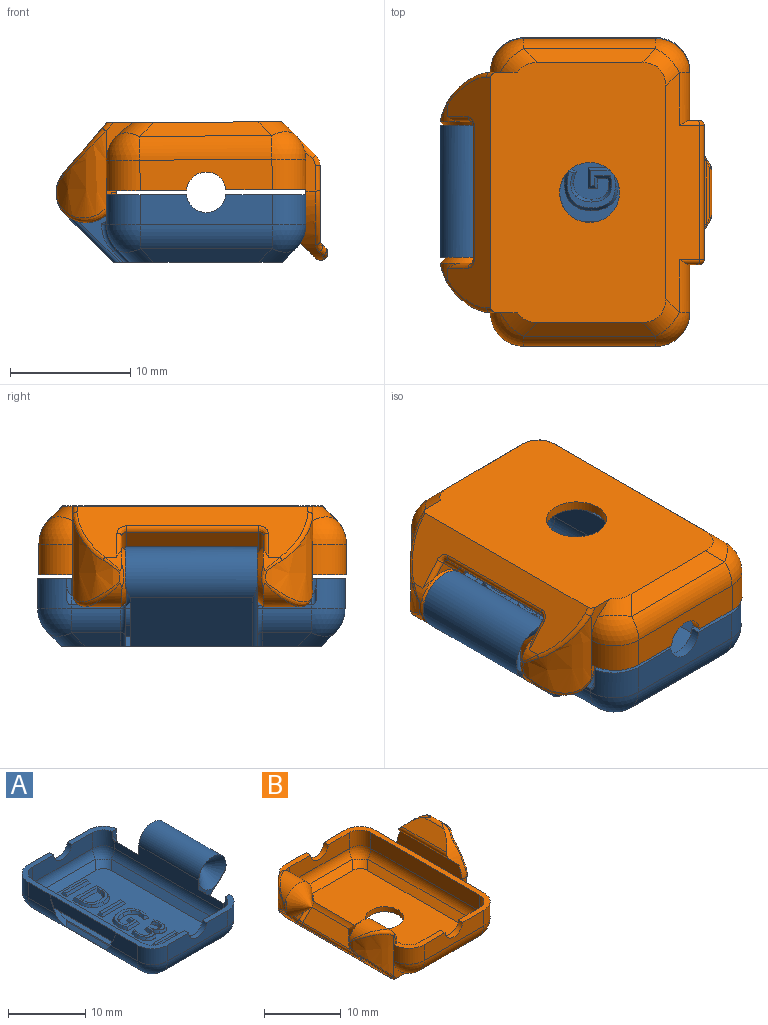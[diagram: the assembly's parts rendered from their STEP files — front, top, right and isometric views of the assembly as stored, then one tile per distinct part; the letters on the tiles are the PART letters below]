
ASSEMBLY  parts=2 mates=1
PART A: 172 faces, bbox 21.2x25.8x8.8 mm
  f0: plane 21.17x12.17mm, normal (0,0,1), area 198.2mm2, adj f18,f19,f20,f21,f22,f23,f24,f25
  f1: cylinder r=2mm len=20mm, axis (0,1,0), area 20.4mm2, adj f4,f21,f36,f38,f69,f71,f72
  f2: cylinder r=2.8mm len=20mm, axis (0,1,0), area 28.1mm2, adj f3,f28,f42,f44,f48,f71,f72,f74
  f3: plane 5.02x2.6mm, normal (-1,0,0), area 11mm2, adj f2,f5,f47,f71
  f4: plane 20x2.52mm, normal (1,0,0), area 50.3mm2, adj f1,f5,f53,f54,f70,f71,f72
  f5: plane 25.6x6.66mm, normal (0,0,1), area 27mm2, adj f3,f4,f46,f47,f48,f49,f50,f51
  f6: plane 4.1x1.15mm, normal (0.71,0,-0.71), area 5.7mm2, adj f10,f17,f30,f167
  f7: plane 4.1x1.15mm, normal (0.71,0,-0.71), area 5.7mm2, adj f11,f17,f32,f162
  f8: plane 4.1x0.32mm, normal (1,0,0), area 1.3mm2, adj f10,f12,f63,f165
  f9: plane 4.1x0.32mm, normal (1,0,0), area 1.3mm2, adj f11,f13,f61,f164
  f10: cylinder r=2.8mm len=4.1mm, axis (0,-1,0), area 9mm2, adj f6,f8,f43,f166
  f11: cylinder r=2.8mm len=4.1mm, axis (0,-1,0), area 9mm2, adj f7,f9,f45,f163
  f12: cylinder r=2.8mm len=2.8mm, axis (0,0,1), area 10.3mm2, adj f8,f43,f49,f58,f64,f171
  f13: cylinder r=2.8mm len=2.8mm, axis (0,0,-1), area 10.3mm2, adj f9,f16,f45,f50,f60,f170
  f14: cylinder r=2mm len=2.52mm, axis (0,0,1), area 7.5mm2, adj f37,f55,f56,f58,f171
  f15: cylinder r=2mm len=2.52mm, axis (0,0,-1), area 7.5mm2, adj f16,f39,f56,f57,f170
  f16: plane 6.63x2.4mm, normal (0,0,1), area 5.8mm2, adj f13,f15,f50,f51,f57,f60,f170
  f17: plane 21.83x14.24mm, normal (0,0,-1), area 286.8mm2, adj f6,f7,f26,f27,f28,f29,f30,f31
  f18: plane 11x0.91mm, normal (0,-0.71,0.71), area 13mm2, adj f0,f24,f25,f33
  f19: plane 20x0.91mm, normal (-0.71,0,0.71), area 24.7mm2, adj f0,f23,f25,f34
  f20: plane 11x0.91mm, normal (0,0.71,0.71), area 13mm2, adj f0,f22,f23,f35
  f21: plane 20x0.91mm, normal (0.71,0,0.71), area 24.7mm2, adj f0,f1,f22,f24
  f22: cylinder r=2mm len=2.33mm, axis (0.58,0.58,-0.58), area 2.8mm2, adj f0,f20,f21,f36
  f23: cylinder r=2mm len=2.33mm, axis (0.58,-0.58,0.58), area 2.8mm2, adj f0,f19,f20,f37
  f24: cylinder r=2mm len=2.33mm, axis (0.58,-0.58,-0.58), area 2.8mm2, adj f0,f18,f21,f38
  f25: cylinder r=2mm len=2.33mm, axis (0.58,0.58,0.58), area 2.8mm2, adj f0,f18,f19,f39
  f26: plane 11x1.15mm, normal (0,0.71,-0.71), area 16mm2, adj f17,f31,f32,f40
  f27: plane 11x1.15mm, normal (0,-0.71,-0.71), area 16mm2, adj f17,f29,f30,f41
  f28: plane 20x1.15mm, normal (-0.71,0,-0.71), area 30.6mm2, adj f2,f17,f29,f31
  f29: cylinder r=2.8mm len=3.13mm, axis (0.58,0.58,-0.58), area 4.8mm2, adj f17,f27,f28,f42
  f30: cylinder r=2.8mm len=3.13mm, axis (0.58,-0.58,0.58), area 4.8mm2, adj f6,f17,f27,f43
  f31: cylinder r=2.8mm len=3.13mm, axis (0.58,-0.58,-0.58), area 4.8mm2, adj f17,f26,f28,f44
  f32: cylinder r=2.8mm len=3.13mm, axis (0.58,0.58,0.58), area 4.8mm2, adj f7,f17,f26,f45
  f33: cylinder r=2mm len=11mm, axis (1,0,0), area 17.3mm2, adj f18,f38,f39,f57
  f34: cylinder r=2mm len=20mm, axis (0,-1,0), area 31.4mm2, adj f19,f37,f39,f56
  f35: cylinder r=2mm len=11mm, axis (-1,0,0), area 17.3mm2, adj f20,f36,f37,f55
  f36: sphere r=2mm, area 4.9mm2, adj f1,f22,f35,f53
  f37: sphere r=2mm, area 4.9mm2, adj f14,f23,f34,f35
  f38: sphere r=2mm, area 4.9mm2, adj f1,f24,f33,f54
  f39: sphere r=2mm, area 4.9mm2, adj f15,f25,f33,f34
  f40: cylinder r=2.8mm len=11mm, axis (1,0,0), area 24.2mm2, adj f26,f44,f45,f50
  f41: cylinder r=2.8mm len=11mm, axis (-1,0,0), area 24.2mm2, adj f27,f42,f43,f49
  f42: sphere r=2.8mm, area 9.7mm2, adj f2,f29,f41,f46
  f43: sphere r=2.8mm, area 9.7mm2, adj f10,f12,f30,f41
  f44: sphere r=2.8mm, area 9.7mm2, adj f2,f31,f40,f47
  f45: sphere r=2.8mm, area 9.7mm2, adj f11,f13,f32,f40
  f46: cylinder r=2.8mm len=2.8mm, axis (0,0,-1), area 11.1mm2, adj f5,f42,f48,f49
  f47: cylinder r=2.8mm len=2.8mm, axis (0,0,1), area 11.1mm2, adj f3,f5,f44,f50
  f48: plane 5.02x2.6mm, normal (-1,0,0), area 11mm2, adj f2,f5,f46,f72
  f49: plane 11x2.52mm, normal (0,-1,0), area 24mm2, adj f5,f12,f41,f46,f52,f58
  f50: plane 11x2.52mm, normal (0,1,0), area 24mm2, adj f5,f13,f16,f40,f47,f51
  f51: cylinder r=1.65mm len=3.29mm, axis (0,1,0), area 3.9mm2, adj f5,f16,f50,f57
  f52: cylinder r=1.65mm len=3.29mm, axis (0,1,0), area 3.9mm2, adj f5,f49,f55,f58
  f53: cylinder r=2mm len=2.52mm, axis (0,0,-1), area 7.9mm2, adj f4,f5,f36,f55
  f54: cylinder r=2mm len=2.52mm, axis (0,0,1), area 7.9mm2, adj f4,f5,f38,f57
  f55: plane 11x2.52mm, normal (0,1,0), area 24mm2, adj f5,f14,f35,f52,f53,f58
  f56: plane 20x2.67mm, normal (-1,0,0), area 40.2mm2, adj f14,f15,f34,f59,f61,f62,f63,f67
  f57: plane 11x2.52mm, normal (0,-1,0), area 24mm2, adj f5,f15,f16,f33,f51,f54
  f58: plane 6.63x2.4mm, normal (0,0,1), area 5.8mm2, adj f12,f14,f49,f52,f55,f64,f171
  f59: plane 5.8x3.63mm, normal (0,1,0), area 3.2mm2, adj f17,f56,f61,f65,f162,f163,f164,f169
  f60: plane 1.66x0.77mm, normal (0,-1,0), area 0.8mm2, adj f13,f16,f170
  f61: cylinder r=2.9mm len=4.5mm, axis (0,1,0), area 5.4mm2, adj f9,f56,f59,f164,f170
  f62: plane 5.8x3.63mm, normal (0,-1,0), area 3.2mm2, adj f17,f56,f63,f66,f165,f166,f167,f168
  f63: cylinder r=2.9mm len=4.5mm, axis (0,1,0), area 5.4mm2, adj f8,f56,f62,f165,f171
  f64: plane 1.66x0.77mm, normal (0,1,0), area 0.8mm2, adj f12,f58,f171
  f65: cone r=2.5mm half-angle=45deg, axis (0,1,0), area 27.5mm2, adj f59,f67,f169
  f66: cone r=2.5mm half-angle=45deg, axis (0,-1,0), area 27.5mm2, adj f62,f67,f168
  f67: cylinder r=2.5mm len=11mm, axis (0,1,0), area 107.4mm2, adj f56,f65,f66,f68,f168,f169
  f68: plane 10.2x4.03mm, normal (0.71,0,-0.71), area 58.2mm2, adj f17,f67,f168,f169
  f69: cylinder r=0.7mm len=8.33mm, axis (0,1,0), area 1.2mm2, adj f1,f71,f72,f74
  f70: plane 10.87x0.71mm, normal (-0.71,0,-0.71), area 10.4mm2, adj f4,f71,f72,f73
  f71: extruded ~4.23x2.39mm, area 2.1mm2, adj f1,f2,f3,f4,f5,f69,f70,f73
  f72: extruded ~4.23x2.39mm, area 2.1mm2, adj f1,f2,f4,f5,f48,f69,f70,f73
  f73: plane 11.99x1.81mm, normal (-1,0,0), area 20.9mm2, adj f5,f70,f71,f72
  f74: plane 8.15x0.49mm, normal (-0.71,0,0.71), area 5.2mm2, adj f2,f69,f71,f72
  f75: plane 4.35x0.4mm, normal (0,0.87,0.5), area 1.9mm2, adj f0,f76,f78,f79
  f76: plane 0.92x0.4mm, normal (-0.87,0,0.5), area 0.3mm2, adj f0,f75,f77,f79
  f77: plane 4.35x0.4mm, normal (0,-0.87,0.5), area 1.9mm2, adj f0,f76,f78,f79
  f78: plane 0.92x0.4mm, normal (0.87,0,0.5), area 0.3mm2, adj f0,f75,f77,f79
  f79: plane 3.89x0.46mm, normal (0,0,1), area 1.8mm2, adj f75,f76,f77,f78
  f80: bspline ~1.68x1.52mm, area 1.1mm2, adj f81,f91,f92,f93
  f81: bspline ~1.71x1.61mm, area 1.1mm2, adj f80,f82,f92,f93
  f82: plane 0.63x0.4mm, normal (0.87,0,0.5), area 0.2mm2, adj f81,f83,f92,f93
  f83: plane 3.3x0.4mm, normal (0,-0.87,0.5), area 1.4mm2, adj f82,f91,f92,f93
  f84: bspline ~1.65x0.8mm, area 0.8mm2, adj f0,f85,f90,f92
  f85: bspline ~1.57x0.78mm, area 0.8mm2, adj f0,f84,f86,f92
  f86: bspline ~1.66x0.76mm, area 0.8mm2, adj f0,f85,f87,f92
  f87: plane 1.37x0.4mm, normal (0.87,0,0.5), area 0.6mm2, adj f0,f86,f88,f92
  f88: plane 4.35x0.4mm, normal (0,0.87,0.5), area 1.9mm2, adj f0,f87,f89,f92
  f89: plane 1.23x0.4mm, normal (-0.87,0,0.5), area 0.5mm2, adj f0,f88,f90,f92
  f90: bspline ~1.77x0.77mm, area 0.8mm2, adj f0,f84,f89,f92
  f91: plane 0.72x0.4mm, normal (-0.87,0,0.5), area 0.3mm2, adj f80,f83,f92,f93
  f92: plane 4.09x3.34mm, normal (0,0,1), area 4.5mm2, adj f80,f81,f82,f83,f84,f85,f86,f87
  f93: plane 3.02x1.91mm, normal (0,0,1), area 4.3mm2, adj f80,f81,f82,f83,f91
  f94: plane 4.35x0.4mm, normal (0,0.87,0.5), area 1.9mm2, adj f0,f95,f97,f98
  f95: plane 0.92x0.4mm, normal (-0.87,0,0.5), area 0.3mm2, adj f0,f94,f96,f98
  f96: plane 4.35x0.4mm, normal (0,-0.87,0.5), area 1.9mm2, adj f0,f95,f97,f98
  f97: plane 0.92x0.4mm, normal (0.87,0,0.5), area 0.3mm2, adj f0,f94,f96,f98
  f98: plane 3.89x0.46mm, normal (0,0,1), area 1.8mm2, adj f94,f95,f96,f97
  f99: plane 1.73x0.4mm, normal (0.87,0,0.5), area 0.7mm2, adj f0,f100,f117,f118
  f100: plane 0.77x0.4mm, normal (0,0.87,0.5), area 0.2mm2, adj f0,f99,f101,f118
  f101: plane 1.06x0.4mm, normal (-0.87,0,0.5), area 0.4mm2, adj f0,f100,f102,f118
  f102: plane 1.34x0.41mm, normal (0,0.87,0.5), area 0.5mm2, adj f0,f101,f103,f118
  f103: bspline ~0.83x0.48mm, area 0.3mm2, adj f0,f102,f104,f118
  f104: bspline ~1.06x0.65mm, area 0.5mm2, adj f0,f103,f105,f118
  f105: bspline ~1.25x0.57mm, area 0.6mm2, adj f0,f104,f106,f118
  f106: bspline ~1.27x0.64mm, area 0.6mm2, adj f0,f105,f107,f118
  f107: bspline ~1.16x0.68mm, area 0.5mm2, adj f0,f106,f108,f118
  f108: bspline ~1.12x0.52mm, area 0.5mm2, adj f0,f107,f109,f118
  f109: plane 0.92x0.61mm, normal (-0.33,-0.8,0.5), area 0.3mm2, adj f0,f108,f110,f118
  f110: bspline ~1.29x0.52mm, area 0.6mm2, adj f0,f109,f111,f118
  f111: bspline ~1.67x0.79mm, area 0.8mm2, adj f0,f110,f112,f118
  f112: bspline ~1.64x0.8mm, area 0.8mm2, adj f0,f111,f113,f118
  f113: bspline ~1.66x0.73mm, area 0.8mm2, adj f0,f112,f114,f118
  f114: bspline ~1.5x0.76mm, area 0.7mm2, adj f0,f113,f115,f118
  f115: bspline ~0.76x0.48mm, area 0.3mm2, adj f0,f114,f116,f118
  f116: bspline ~0.83x0.48mm, area 0.4mm2, adj f0,f115,f117,f118
  f117: plane 2.44x0.58mm, normal (0,-0.87,0.5), area 0.9mm2, adj f0,f99,f116,f118
  f118: plane 4.2x3.3mm, normal (0,0,1), area 4.1mm2, adj f99,f100,f101,f102,f103,f104,f105,f106
  f119: plane 2.74x2.47mm, normal (0,0,1), area 1.6mm2, adj f129,f130,f131,f132,f133,f134,f135,f136
  f120: bspline ~0.69x0.48mm, area 0.3mm2, adj f0,f121,f146,f147
  f121: bspline ~0.76x0.55mm, area 0.4mm2, adj f0,f120,f122,f147
  f122: bspline ~1.07x0.5mm, area 0.5mm2, adj f0,f121,f123,f147
  f123: bspline ~1.42x0.65mm, area 0.7mm2, adj f0,f122,f124,f147
  f124: plane 0.82x0.68mm, normal (-0.48,0.72,0.5), area 0.2mm2, adj f0,f123,f125,f147
  f125: bspline ~0.64x0.51mm, area 0.2mm2, adj f0,f124,f126,f147
  f126: bspline ~0.52x0.48mm, area 0.2mm2, adj f0,f125,f127,f147
  f127: bspline ~0.9x0.77mm, area 0.5mm2, adj f0,f126,f128,f147
  f128: bspline ~0.69x0.51mm, area 0.3mm2, adj f0,f127,f129,f147
  f129: bspline ~0.88x0.48mm, area 0.4mm2, adj f0,f119,f128,f130,f145,f146,f147
  f130: plane 0.4x0.34mm, normal (0.87,0,0.5), area 0.1mm2, adj f0,f119,f129,f131
  f131: plane 0.71x0.4mm, normal (0,0.87,0.5), area 0.2mm2, adj f0,f119,f130,f132
  f132: plane 0.4x0.33mm, normal (-0.87,0,0.5), area 0.1mm2, adj f0,f119,f131,f133
  f133: bspline ~0.92x0.48mm, area 0.4mm2, adj f0,f119,f132,f134
  f134: bspline ~0.68x0.53mm, area 0.3mm2, adj f0,f119,f133,f135
  f135: bspline ~0.72x0.49mm, area 0.3mm2, adj f0,f119,f134,f136
  f136: bspline ~0.83x0.48mm, area 0.4mm2, adj f0,f119,f135,f137
  f137: bspline ~0.67x0.48mm, area 0.3mm2, adj f0,f119,f136,f138
  f138: bspline ~0.68x0.48mm, area 0.2mm2, adj f0,f119,f137,f139
  f139: plane 0.97x0.58mm, normal (0,0.87,0.5), area 0.2mm2, adj f0,f119,f138,f140
  f140: bspline ~1.26x0.49mm, area 0.6mm2, adj f0,f119,f139,f141
  f141: bspline ~1.3x0.57mm, area 0.6mm2, adj f0,f119,f140,f142
  f142: bspline ~0.98x0.62mm, area 0.5mm2, adj f0,f119,f141,f143
  f143: bspline ~0.69x0.48mm, area 0.3mm2, adj f0,f119,f142,f144
  f144: bspline ~1.04x0.55mm, area 0.4mm2, adj f0,f119,f143,f145
  f145: plane 0.43x0.43mm, normal (0,-0.87,0.5), area 0.1mm2, adj f0,f119,f129,f144,f146
  f146: bspline ~0.94x0.62mm, area 0.4mm2, adj f0,f120,f129,f145,f147
  f147: plane 2.51x1.87mm, normal (0,0,1), area 1.1mm2, adj f120,f121,f122,f123,f124,f125,f126,f127
  f148: bspline ~1.68x1.52mm, area 1.1mm2, adj f149,f159,f160,f161
  f149: bspline ~1.71x1.61mm, area 1.1mm2, adj f148,f150,f160,f161
  f150: plane 0.63x0.4mm, normal (0.87,0,0.5), area 0.2mm2, adj f149,f151,f160,f161
  f151: plane 3.3x0.4mm, normal (0,-0.87,0.5), area 1.4mm2, adj f150,f159,f160,f161
  f152: bspline ~1.65x0.8mm, area 0.8mm2, adj f0,f153,f158,f160
  f153: bspline ~1.57x0.78mm, area 0.8mm2, adj f0,f152,f154,f160
  f154: bspline ~1.66x0.76mm, area 0.8mm2, adj f0,f153,f155,f160
  f155: plane 1.37x0.4mm, normal (0.87,0,0.5), area 0.6mm2, adj f0,f154,f156,f160
  f156: plane 4.35x0.4mm, normal (0,0.87,0.5), area 1.9mm2, adj f0,f155,f157,f160
  f157: plane 1.23x0.4mm, normal (-0.87,0,0.5), area 0.5mm2, adj f0,f156,f158,f160
  f158: bspline ~1.77x0.77mm, area 0.8mm2, adj f0,f152,f157,f160
  f159: plane 0.72x0.4mm, normal (-0.87,0,0.5), area 0.3mm2, adj f148,f151,f160,f161
  f160: plane 4.09x3.34mm, normal (0,0,1), area 4.5mm2, adj f148,f149,f150,f151,f152,f153,f154,f155
  f161: plane 3.02x1.91mm, normal (0,0,1), area 4.3mm2, adj f148,f149,f150,f151,f159
  f162: cylinder r=0.4mm len=1.43mm, axis (0.71,0,0.71), area 0.9mm2, adj f7,f17,f59,f163
  f163: torus R=3.2mm, axis (0,1,0), area 1.5mm2, adj f11,f59,f162,f164
  f164: cylinder r=0.4mm len=0.4mm, axis (0,0,1), area 0.1mm2, adj f9,f59,f61,f163
  f165: cylinder r=0.4mm len=0.4mm, axis (0,0,1), area 0.1mm2, adj f8,f62,f63,f166
  f166: torus R=3.2mm, axis (0,1,0), area 1.5mm2, adj f10,f62,f165,f167
  f167: cylinder r=0.4mm len=1.43mm, axis (0.71,0,0.71), area 0.9mm2, adj f6,f17,f62,f166
  f168: cylinder r=0.4mm len=5.56mm, axis (-0.71,0,-0.71), area 3.5mm2, adj f17,f62,f66,f67,f68
  f169: cylinder r=0.4mm len=5.56mm, axis (-0.71,0,-0.71), area 3.5mm2, adj f17,f59,f65,f67,f68
  f170: torus R=2.5mm, axis (0,-1,0), area 0.9mm2, adj f13,f15,f16,f60,f61
  f171: torus R=2.5mm, axis (0,-1,0), area 0.9mm2, adj f12,f14,f58,f63,f64
PART B: 122 faces, bbox 24.2x26.7x12.9 mm
  f0: plane 19.29x4.24mm, normal (-0.75,0,-0.66), area 55.2mm2, adj f2,f17,f18,f99,f100,f106,f107,f115
  f1: cylinder r=2.5mm len=4.94mm, axis (0,1,0), area 19.8mm2, adj f5,f24,f102,f103,f104
  f2: cylinder r=2.5mm len=1.86mm, axis (0,1,0), area 1.2mm2, adj f0,f5,f101,f102,f121
  f3: cylinder r=2.5mm len=4.94mm, axis (0,1,0), area 19.8mm2, adj f22,f24,f109,f110,f111
  f4: plane 3.16x2.29mm, normal (0,1,0), area 2mm2, adj f17,f67,f69,f81,f99
  f5: cone r=2.5mm half-angle=45deg, axis (0,1,0), area 27.8mm2, adj f1,f2,f73,f102,f116
  f6: plane 3.16x2.29mm, normal (0,-1,0), area 2mm2, adj f17,f62,f64,f80,f106
  f7: plane 12x2.18mm, normal (-1,0,0), area 25mm2, adj f12,f14,f72,f76,f77,f78
  f8: plane 5.15x0.31mm, normal (0.71,0,-0.71), area 2mm2, adj f9,f88,f92,f93
  f9: cylinder r=0.6mm len=4.18mm, axis (0,1,0), area 5.7mm2, adj f8,f10,f77,f78,f86,f90
  f10: plane 8.62x2.13mm, normal (-0.71,0,0.71), area 15.8mm2, adj f9,f11,f77,f78
  f11: cylinder r=0.6mm len=9.6mm, axis (0,1,0), area 8.4mm2, adj f10,f12,f77,f78
  f12: plane 10.83x1mm, normal (-0.71,0,-0.71), area 14.3mm2, adj f7,f11,f77,f78
  f13: plane 11.2x6.3mm, normal (1,0,0), area 63.5mm2, adj f75,f87,f89,f93,f95,f96
  f14: plane 3.35x0.88mm, normal (0,1,0), area 2.3mm2, adj f7,f15,f16,f77,f84,f85,f87
  f15: plane 4x2.52mm, normal (1,0,0), area 10.1mm2, adj f14,f16,f38,f72
  f16: cylinder r=2.8mm len=4.4mm, axis (0,1,0), area 9.1mm2, adj f14,f15,f59,f68,f84
  f17: plane 22.72x15.63mm, normal (0,0,-1), area 290mm2, adj f0,f4,f6,f57,f58,f59,f60,f62
  f18: cylinder r=2.5mm len=1.86mm, axis (0,1,0), area 1.2mm2, adj f0,f22,f108,f109,f115
  f19: plane 1.38x0.4mm, normal (0,1,0), area 0.4mm2, adj f20,f81,f104,f105
  f20: plane 6.66x3.2mm, normal (0,0,1), area 6.1mm2, adj f19,f23,f24,f30,f32,f33,f39,f105
  f21: plane 1.38x0.4mm, normal (0,-1,0), area 0.4mm2, adj f71,f80,f111,f112
  f22: cone r=2.5mm half-angle=45deg, axis (0,-1,0), area 27.8mm2, adj f3,f18,f74,f109,f113
  f23: plane 11x2.52mm, normal (0,-1,0), area 24mm2, adj f20,f29,f30,f32,f56,f72
  f24: plane 20.47x3.14mm, normal (1,0,0), area 36.1mm2, adj f1,f3,f20,f28,f30,f52,f71,f82
  f25: plane 11x2.52mm, normal (0,1,0), area 24mm2, adj f27,f28,f31,f46,f71,f72
  f26: plane 20x2.52mm, normal (-1,0,0), area 50.4mm2, adj f27,f29,f51,f72
  f27: cylinder r=2mm len=2.52mm, axis (0,0,1), area 7.9mm2, adj f25,f26,f48,f72
  f28: cylinder r=2mm len=2.52mm, axis (0,0,-1), area 7.9mm2, adj f24,f25,f49,f71
  f29: cylinder r=2mm len=2.52mm, axis (0,0,-1), area 7.9mm2, adj f23,f26,f54,f72
  f30: cylinder r=2mm len=2.52mm, axis (0,0,1), area 7.9mm2, adj f20,f23,f24,f55
  f31: cylinder r=1.65mm len=3.29mm, axis (0,1,0), area 3.9mm2, adj f25,f34,f71,f72
  f32: cylinder r=1.65mm len=3.29mm, axis (0,1,0), area 3.9mm2, adj f20,f23,f33,f72
  f33: plane 11x2.52mm, normal (0,1,0), area 24mm2, adj f20,f32,f38,f39,f70,f72
  f34: plane 11x2.52mm, normal (0,-1,0), area 24mm2, adj f31,f36,f37,f61,f71,f72
  f35: plane 4x2.52mm, normal (1,0,0), area 10.1mm2, adj f36,f66,f72,f76
  f36: cylinder r=2.8mm len=2.8mm, axis (0,0,1), area 11.1mm2, adj f34,f35,f63,f72
  f37: cylinder r=2.8mm len=2.8mm, axis (0,0,-1), area 11.1mm2, adj f34,f64,f71,f80
  f38: cylinder r=2.8mm len=2.8mm, axis (0,0,-1), area 11.1mm2, adj f15,f33,f68,f72
  f39: cylinder r=2.8mm len=2.8mm, axis (0,0,1), area 11.1mm2, adj f20,f33,f69,f81
  f40: plane 21.76x12.76mm, normal (0,0,1), area 230.9mm2, adj f41,f42,f43,f44,f45,f47,f50,f53
  f41: plane 20x0.91mm, normal (0.71,0,0.71), area 24.7mm2, adj f40,f47,f52,f53
  f42: plane 11x0.91mm, normal (0,-0.71,0.71), area 13mm2, adj f40,f50,f53,f56
  f43: plane 11x0.91mm, normal (0,0.71,0.71), area 13mm2, adj f40,f45,f46,f47
  f44: plane 20x0.91mm, normal (-0.71,0,0.71), area 24.7mm2, adj f40,f45,f50,f51
  f45: cylinder r=2mm len=2.33mm, axis (0.58,-0.58,0.58), area 3.3mm2, adj f40,f43,f44,f48
  f46: cylinder r=2mm len=11mm, axis (1,0,0), area 17.3mm2, adj f25,f43,f48,f49
  f47: cylinder r=2mm len=2.33mm, axis (0.58,0.58,-0.58), area 3.3mm2, adj f40,f41,f43,f49
  f48: sphere r=2mm, area 4.9mm2, adj f27,f45,f46,f51
  f49: sphere r=2mm, area 4.4mm2, adj f28,f46,f47,f52
  f50: cylinder r=2mm len=2.33mm, axis (0.58,0.58,0.58), area 3.3mm2, adj f40,f42,f44,f54
  f51: cylinder r=2mm len=20mm, axis (0,1,0), area 31.4mm2, adj f26,f44,f48,f54
  f52: cylinder r=2mm len=20mm, axis (0,-1,0), area 31.4mm2, adj f24,f41,f49,f55
  f53: cylinder r=2mm len=2.33mm, axis (0.58,-0.58,-0.58), area 3.3mm2, adj f40,f41,f42,f55
  f54: sphere r=2mm, area 4.4mm2, adj f29,f50,f51,f56
  f55: sphere r=2mm, area 4.4mm2, adj f30,f52,f53,f56
  f56: cylinder r=2mm len=11mm, axis (-1,0,0), area 17.3mm2, adj f23,f42,f54,f55
  f57: plane 11x1.15mm, normal (0,0.71,-0.71), area 16mm2, adj f17,f65,f67,f70
  f58: plane 11x1.15mm, normal (0,-0.71,-0.71), area 16mm2, adj f17,f60,f61,f62
  f59: plane 20x2.82mm, normal (0.71,0,-0.71), area 57mm2, adj f16,f17,f60,f65,f66,f75,f84,f98
  f60: cylinder r=2.8mm len=3.13mm, axis (0.58,-0.58,0.58), area 5.8mm2, adj f17,f58,f59,f63
  f61: cylinder r=2.8mm len=11mm, axis (1,0,0), area 24.2mm2, adj f34,f58,f63,f64
  f62: cylinder r=2.8mm len=3.13mm, axis (0.58,0.58,-0.58), area 4mm2, adj f6,f17,f58,f64
  f63: sphere r=2.8mm, area 9.7mm2, adj f36,f60,f61,f66
  f64: sphere r=2.8mm, area 8.7mm2, adj f6,f37,f61,f62
  f65: cylinder r=2.8mm len=3.13mm, axis (0.58,0.58,0.58), area 5.8mm2, adj f17,f57,f59,f68
  f66: cylinder r=2.8mm len=4.4mm, axis (0,1,0), area 9.1mm2, adj f35,f59,f63,f76,f98
  f67: cylinder r=2.8mm len=3.13mm, axis (0.58,-0.58,-0.58), area 4mm2, adj f4,f17,f57,f69
  f68: sphere r=2.8mm, area 8.7mm2, adj f16,f38,f65,f70
  f69: sphere r=2.8mm, area 8.7mm2, adj f4,f39,f67,f70
  f70: cylinder r=2.8mm len=11mm, axis (-1,0,0), area 24.2mm2, adj f33,f57,f68,f69
  f71: plane 6.66x3.2mm, normal (0,0,1), area 6.1mm2, adj f21,f24,f25,f28,f31,f34,f37,f112
  f72: plane 25.6x6.66mm, normal (0,0,1), area 28.2mm2, adj f7,f15,f23,f25,f26,f27,f29,f31
  f73: plane 2.45x1.6mm, normal (0,-1,0), area 0.9mm2, adj f5,f118,f121
  f74: plane 2.45x1.6mm, normal (0,1,0), area 0.9mm2, adj f22,f114,f115
  f75: cylinder r=1.2mm len=11.2mm, axis (0,1,0), area 10.6mm2, adj f13,f59,f85,f97
  f76: plane 3.35x0.88mm, normal (0,-1,0), area 2.3mm2, adj f7,f35,f66,f78,f96,f97,f98
  f77: extruded ~5.78x5mm, area 8.7mm2, adj f7,f9,f10,f11,f12,f14,f86,f88
  f78: extruded ~5.78x5mm, area 8.7mm2, adj f7,f9,f10,f11,f12,f76,f90,f92
  f79: cylinder r=2.5mm len=5mm, axis (0,0,1), area 12.6mm2, adj f17,f40
  f80: extruded ~7.22x4.14mm, area 25.7mm2, adj f6,f21,f37,f107,f108,f109,f110
  f81: extruded ~7.22x4.14mm, area 25.7mm2, adj f4,f19,f39,f100,f101,f102,f103
  f82: cylinder r=2.9mm len=11mm, axis (0,1,0), area 8.1mm2, adj f24,f83,f113,f116
  f83: plane 11x1.64mm, normal (-0.71,0,0.71), area 25.5mm2, adj f82,f114,f118,f119
  f84: cylinder r=0.4mm len=1.95mm, axis (-0.71,0,-0.71), area 1mm2, adj f14,f16,f59,f85
  f85: torus R=0.8mm, axis (0,-1,0), area 0.5mm2, adj f14,f75,f84,f87
  f86: bspline ~1.8x1.09mm, area 0.5mm2, adj f9,f77,f88
  f87: cylinder r=0.4mm len=2.13mm, axis (0,0,1), area 1.3mm2, adj f13,f14,f85,f89
  f88: bspline ~1.59x1.44mm, area 0.6mm2, adj f8,f77,f86,f91
  f89: bspline ~6.95x3.35mm, area 3.2mm2, adj f13,f77,f87,f91
  f90: bspline ~1.8x1.09mm, area 0.5mm2, adj f9,f78,f92
  f91: bspline ~1.28x1.1mm, area 0.6mm2, adj f77,f88,f89,f93
  f92: bspline ~1.59x1.44mm, area 0.6mm2, adj f8,f78,f90,f94
  f93: cylinder r=0.4mm len=6.51mm, axis (0,1,0), area 1.8mm2, adj f8,f13,f91,f94
  f94: bspline ~1.12x1.01mm, area 0.6mm2, adj f78,f92,f93,f95
  f95: bspline ~6.95x3.35mm, area 3.2mm2, adj f13,f78,f94,f96
  f96: cylinder r=0.4mm len=2.13mm, axis (0,0,-1), area 1.3mm2, adj f13,f76,f95,f97
  f97: torus R=0.8mm, axis (0,-1,0), area 0.5mm2, adj f75,f76,f96,f98
  f98: cylinder r=0.4mm len=1.95mm, axis (0.71,0,0.71), area 1mm2, adj f59,f66,f76,f97
  f99: cylinder r=0.4mm len=0.94mm, axis (0.66,0,-0.75), area 0.5mm2, adj f0,f4,f17,f100
  f100: bspline ~4.41x4.04mm, area 2.7mm2, adj f0,f81,f99,f101
  f101: bspline ~1.94x1.56mm, area 0.4mm2, adj f2,f81,f100,f102
  f102: bspline ~2.81x0.73mm, area 0.6mm2, adj f1,f2,f5,f81,f101,f103
  f103: bspline ~4.6x4.4mm, area 3.4mm2, adj f1,f81,f102,f104
  f104: torus R=2.1mm, axis (0,-1,0), area 0.9mm2, adj f1,f19,f103,f105
  f105: cylinder r=0.4mm len=0.4mm, axis (0,0,1), area 0.1mm2, adj f19,f20,f24,f104
  f106: cylinder r=0.4mm len=0.94mm, axis (-0.66,0,0.75), area 0.5mm2, adj f0,f6,f17,f107
  f107: bspline ~4.41x4.04mm, area 2.7mm2, adj f0,f80,f106,f108
  f108: bspline ~1.94x1.56mm, area 0.4mm2, adj f18,f80,f107,f109
  f109: bspline ~2.81x0.73mm, area 0.6mm2, adj f3,f18,f22,f80,f108,f110
  f110: bspline ~4.6x4.4mm, area 3.4mm2, adj f3,f80,f109,f111
  f111: torus R=2.1mm, axis (0,-1,0), area 0.9mm2, adj f3,f21,f110,f112
  f112: cylinder r=0.4mm len=0.4mm, axis (0,0,-1), area 0.1mm2, adj f21,f24,f71,f111
  f113: torus R=2.5mm, axis (0,1,0), area 0.9mm2, adj f22,f24,f82,f114
  f114: cylinder r=0.4mm len=1.92mm, axis (0.71,0,0.71), area 1.4mm2, adj f74,f83,f113,f117
  f115: cylinder r=0.4mm len=2.25mm, axis (-0.66,0,0.75), area 1.2mm2, adj f0,f18,f74,f117
  f116: torus R=2.5mm, axis (0,1,0), area 0.9mm2, adj f5,f24,f82,f118
  f117: bspline ~0.94x0.92mm, area 0.5mm2, adj f0,f114,f115,f119
  f118: cylinder r=0.4mm len=1.92mm, axis (0.71,0,0.71), area 1.4mm2, adj f73,f83,f116,f120
  f119: cylinder r=0.4mm len=11mm, axis (0,1,0), area 6.6mm2, adj f0,f83,f117,f120
  f120: bspline ~0.92x0.84mm, area 0.5mm2, adj f0,f118,f119,f121
  f121: cylinder r=0.4mm len=2.25mm, axis (-0.66,0,0.75), area 1.2mm2, adj f0,f2,f73,f120
PLACE A rot(axis=(0,0,1),180deg) t=(0,0,5)mm
PLACE B rot(axis=(1,0,0),180deg) t=(20,-0.1,5.08)mm
MATE revolute A.f61 <-> B.f5  axis (0,-1,0) through (10,0,5)mm
